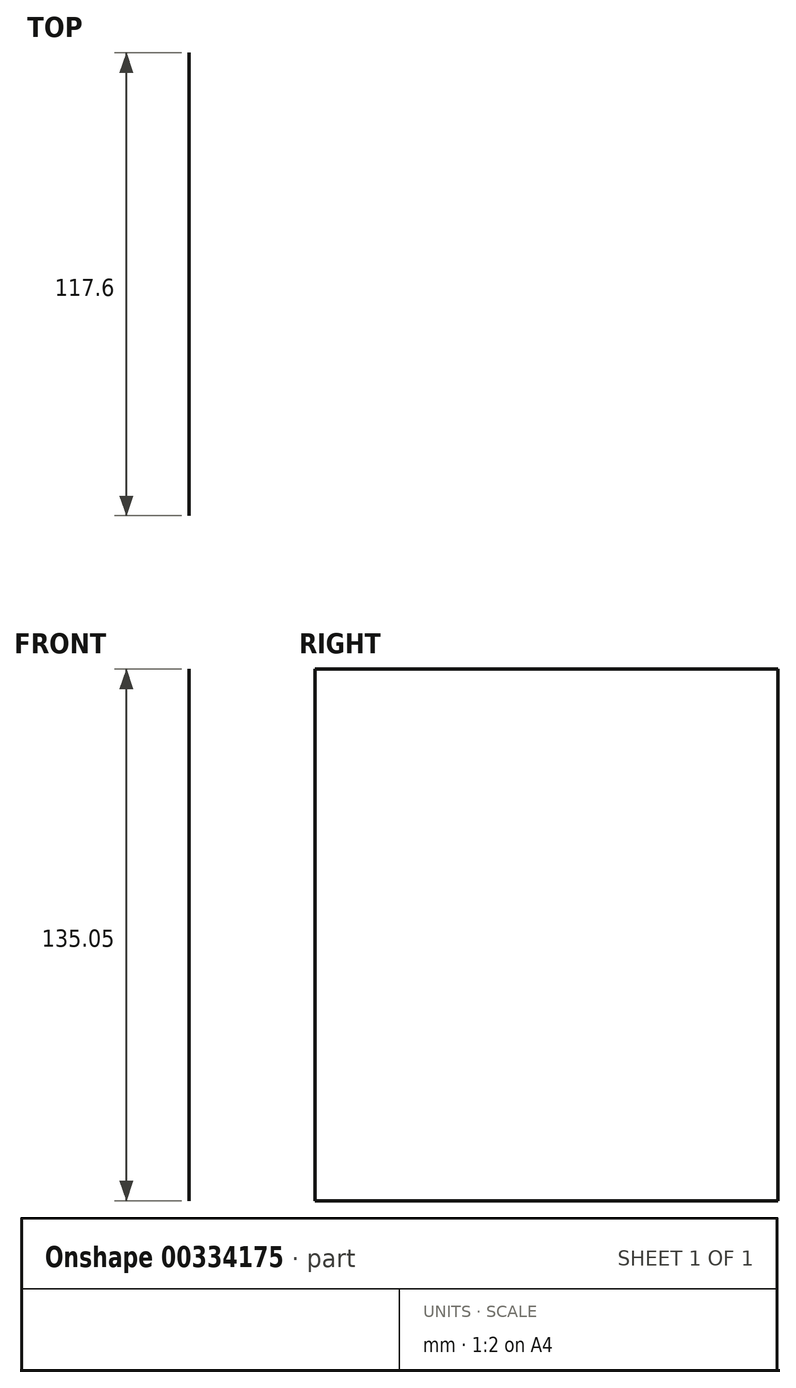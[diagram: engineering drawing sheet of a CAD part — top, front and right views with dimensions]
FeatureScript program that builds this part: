
annotation { "Feature Type Name" : "Feature", "Feature Type Description" : "" }
export const myFeature = defineFeature(function(context is Context, id is Id, definition is map)
    precondition{}
    {
        {
            var Q0;
            Q0=qCreatedBy(makeId("Front.planeOp"),FACE);
            var sketch = newSketch(context, id + "F0", { "sketchPlane" : qUnion([Q0])});
            skLineSegment(sketch, "E0", {"start": v(-166.2, 65.75) * mm, "end": v(-166.2, -69.3) * mm});
            skLineSegment(sketch, "E1", {"start": v(-166.2, -69.3) * mm, "end": v(95.27, -69.3) * mm});
            skLineSegment(sketch, "E2", {"start": v(95.27, -69.3) * mm, "end": v(95.27, 66.4) * mm});
            skLineSegment(sketch, "E3", {"start": v(95.27, 66.4) * mm, "end": v(-166.2, 66.4) * mm});
            skSolve(sketch);
        }
        {
            var Q0;
            Q0=sQuery(id+"F0.wireOp",EDGE,"E0");
            extrude(context, id + "F1", {"bodyType" : ToolBodyType.SURFACE, "surfaceEntities" : qUnion([Q0]), "depth" : 117.6 * mm});
        }
    });
